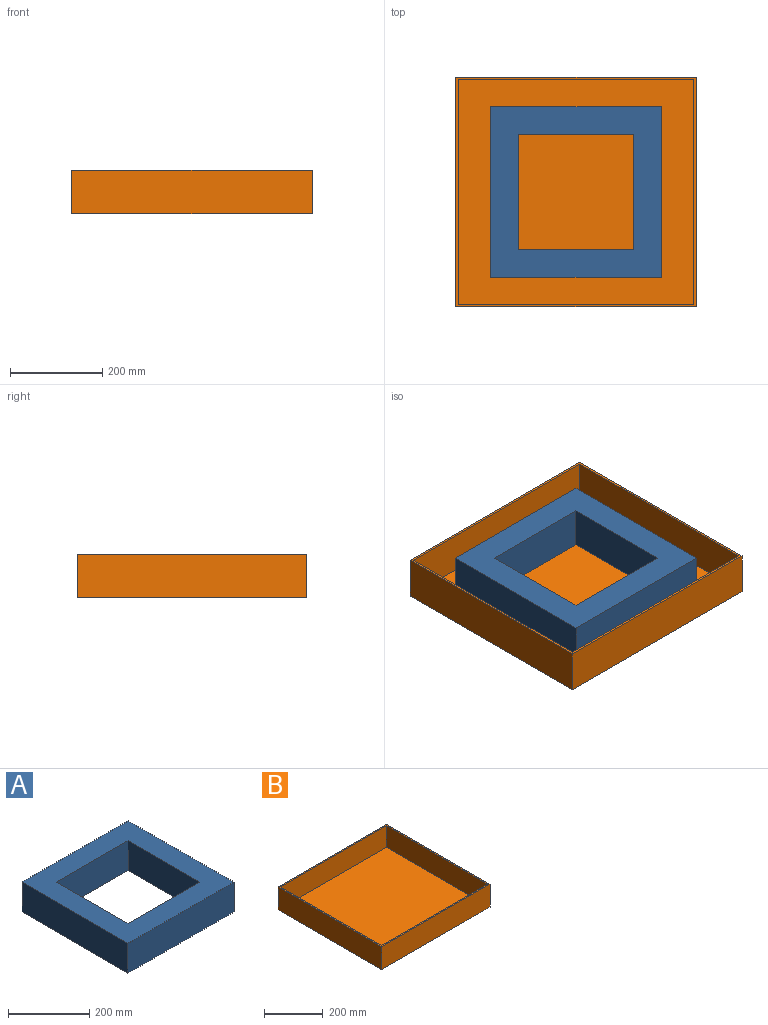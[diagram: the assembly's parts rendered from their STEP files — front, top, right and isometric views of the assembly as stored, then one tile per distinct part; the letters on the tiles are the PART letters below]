
ASSEMBLY  parts=2 mates=1
PART A: 10 faces, bbox 370x370x90 mm
  f0: plane 370x90mm, normal (0,-1,0), area 33300mm2, adj f1,f7,f8,f9
  f1: plane 370x90mm, normal (1,0,0), area 33300mm2, adj f0,f2,f8,f9
  f2: plane 370x90mm, normal (0,1,0), area 33300mm2, adj f1,f7,f8,f9
  f3: plane 250x90mm, normal (-1,0,0), area 22500mm2, adj f4,f6,f8,f9
  f4: plane 250x90mm, normal (0,1,0), area 22500mm2, adj f3,f5,f8,f9
  f5: plane 250x90mm, normal (1,0,0), area 22500mm2, adj f4,f6,f8,f9
  f6: plane 250x90mm, normal (0,-1,0), area 22500mm2, adj f3,f5,f8,f9
  f7: plane 370x90mm, normal (-1,0,0), area 33300mm2, adj f0,f2,f8,f9
  f8: plane 370x370mm, normal (0,0,1), area 74400mm2, adj f0,f1,f2,f3,f4,f5,f6,f7
  f9: plane 370x370mm, normal (0,0,-1), area 74400mm2, adj f0,f1,f2,f3,f4,f5,f6,f7
PART B: 11 faces, bbox 520x497x95 mm
  f0: plane 520x497mm, normal (0,0,1), area 10070mm2, adj f1,f2,f3,f4,f6,f7,f8,f9
  f1: plane 520x95mm, normal (0,-1,0), area 49400mm2, adj f0,f2,f4,f5
  f2: plane 497x95mm, normal (1,0,0), area 47215mm2, adj f0,f1,f3,f5
  f3: plane 520x95mm, normal (0,1,0), area 49400mm2, adj f0,f2,f4,f5
  f4: plane 497x95mm, normal (-1,0,0), area 47215mm2, adj f0,f1,f3,f5
  f5: plane 520x497mm, normal (0,0,-1), area 258440mm2, adj f1,f2,f3,f4
  f6: plane 510x90mm, normal (0,1,0), area 45900mm2, adj f0,f7,f9,f10
  f7: plane 487x90mm, normal (-1,0,0), area 43830mm2, adj f0,f6,f8,f10
  f8: plane 510x90mm, normal (0,-1,0), area 45900mm2, adj f0,f7,f9,f10
  f9: plane 487x90mm, normal (1,0,0), area 43830mm2, adj f0,f6,f8,f10
  f10: plane 510x487mm, normal (0,0,1), area 248370mm2, adj f6,f7,f8,f9
PLACE A rot(axis=(0,0,1),0deg) t=(-539.31,595.21,567.53)mm
PLACE B t=(-472.96,520.3,562.53)mm
MATE parallel B.f10 <-> A.f9  axis (0,0,1) through (-658.07,723.82,567.53)mm
